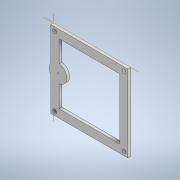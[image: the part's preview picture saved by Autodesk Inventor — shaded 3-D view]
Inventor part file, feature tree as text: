
AUTODESK INVENTOR PART (.ipt)
format: ipt  version: 2022 (Build 260153000, 153)  size: 178,176 bytes
history: native  units: mm
features: other x1, sketch x1, extrude x1
ambient origin geometry x8: Origin, YZ Plane, XZ Plane, XY Plane, X Axis, Y Axis, Z Axis, Center Point
bodies: Body1 (feature_tree)
feature tree (3):
  other  "Sólido1"
  sketch  "Boceto1"  dims[d8=5.0mm d9=0.0mm d11=2.0mm]
  extrude  "Extrusión1"  Depth=5.0mm
